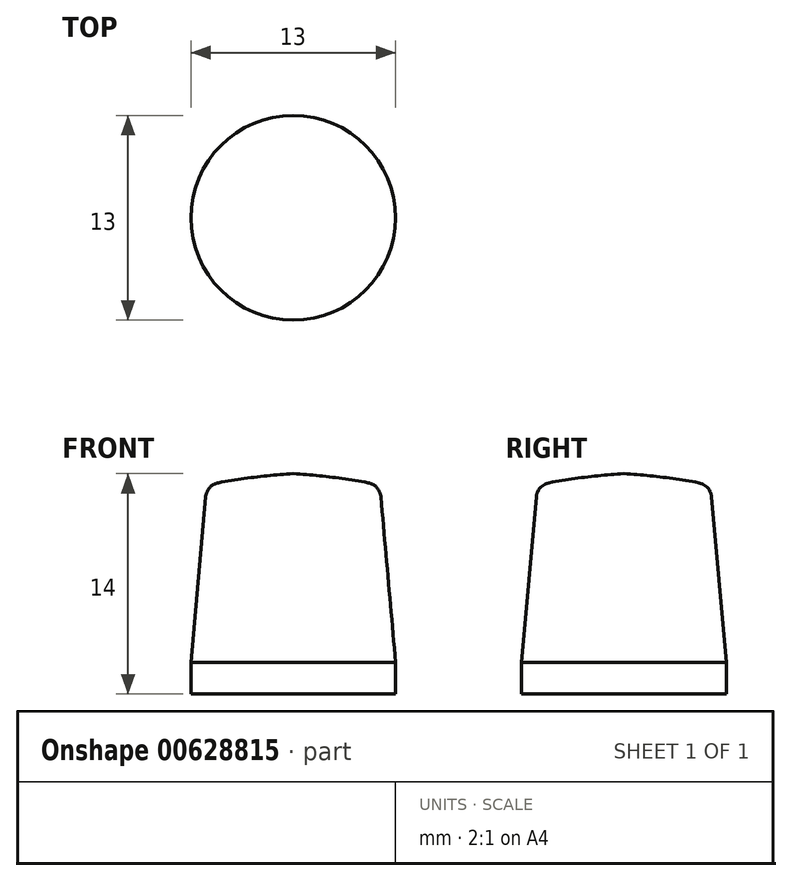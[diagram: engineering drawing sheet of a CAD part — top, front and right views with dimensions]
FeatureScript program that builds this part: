
annotation { "Feature Type Name" : "Feature", "Feature Type Description" : "" }
export const myFeature = defineFeature(function(context is Context, id is Id, definition is map)
    precondition{}
    {
        {
            var Q0;
            Q0=qCreatedBy(makeId("Front.planeOp"),FACE);
            var sketch = newSketch(context, id + "F0", { "sketchPlane" : qUnion([Q0])});
            skLineSegment(sketch, "E0", {"start": v(0, 72.87) * mm, "end": v(0, -65.08) * mm, "construction": true});
            skLineSegment(sketch, "E1", {"start": v(-6.5, -5) * mm, "end": v(-5.57, 5.53) * mm});
            skLineSegment(sketch, "E2", {"start": v(-6.5, -5) * mm, "end": v(-6.5, -7) * mm});
            skLineSegment(sketch, "E3", {"start": v(-6.5, -7) * mm, "end": v(0, -7) * mm});
            skLineSegment(sketch, "E4", {"start": v(0, -7) * mm, "end": v(0, 7) * mm});
            skArc(sketch, "E5", {"start": v(0, 7) * mm, "mid": v(-2.39, 6.79) * mm, "end": v(-4.75, 6.42) * mm});
            skPoint(sketch, "E6.visualSharp", {"position": v(-5.5, 6.27) * mm});
            skArc(sketch, "E6.filletArc", {"start": v(-4.75, 6.42) * mm, "mid": v(-5.31, 6.1) * mm, "end": v(-5.57, 5.53) * mm});
            skSolve(sketch);
        }
        {
            var Q0;
            Q0 = qSketchRegion(id + "F0", true);
            var Q1;
            Q1=sQuery(id+"F0.wireOp",EDGE,"E0");
            revolve(context, id + "F1", {"entities" : qUnion([Q0]), "axis" : qUnion([Q1]), "revolveType" : RevolveType.FULL});
        }
    });
